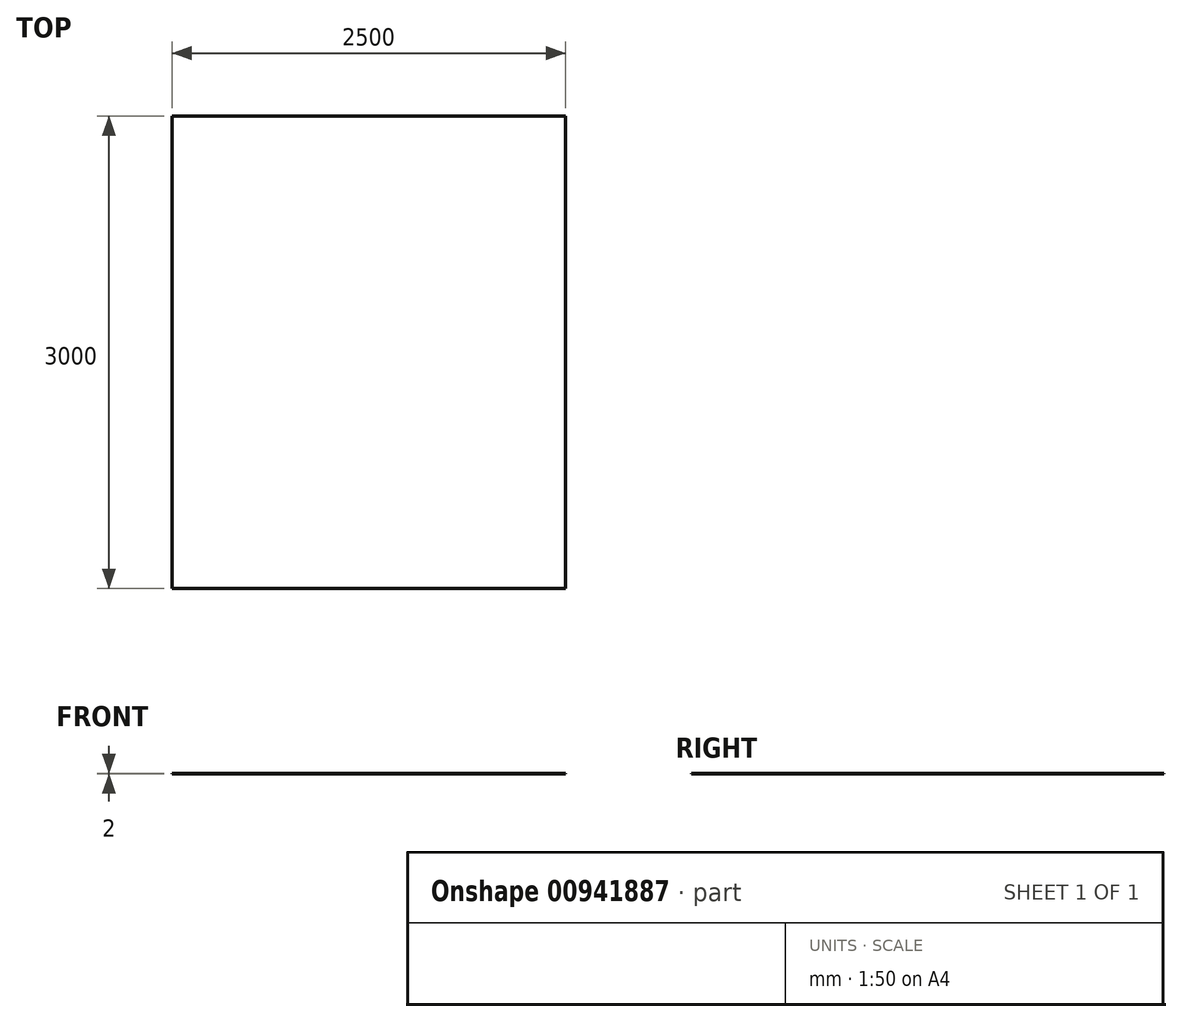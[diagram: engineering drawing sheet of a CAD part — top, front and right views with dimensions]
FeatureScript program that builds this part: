
annotation { "Feature Type Name" : "Feature", "Feature Type Description" : "" }
export const myFeature = defineFeature(function(context is Context, id is Id, definition is map)
    precondition{}
    {
        {
            var Q0;
            Q0=qCreatedBy(makeId("Top.planeOp"),FACE);
            var sketch = newSketch(context, id + "F0", { "sketchPlane" : qUnion([Q0])});
            skLineSegment(sketch, "E0.bottom", {"start": v(1250, 1500) * mm, "end": v(-1250, 1500) * mm});
            skLineSegment(sketch, "E0.top", {"start": v(1250, -1500) * mm, "end": v(-1250, -1500) * mm});
            skLineSegment(sketch, "E0.left", {"start": v(1250, 1500) * mm, "end": v(1250, -1500) * mm});
            skLineSegment(sketch, "E0.right", {"start": v(-1250, 1500) * mm, "end": v(-1250, -1500) * mm});
            skPoint(sketch, "E0.middle", {"position": v(0, 0) * mm});
            skSolve(sketch);
        }
        {
            var Q0;
            Q0=makeQuery(id+"F0.imprint","IMPRINT",FACE,{"disambiguationData":[TD([[makeQuery(id+"F0.imprint","IMPRINT",EDGE,{"derivedFrom":sQuery(id+"F0.wireOp",EDGE,"E0.bottom")}),1.0]])]});
            extrude(context, id + "F1", {"entities" : qUnion([Q0]), "depth" : 2 * mm, "offsetDistance" : 25 * mm});
        }
    });
